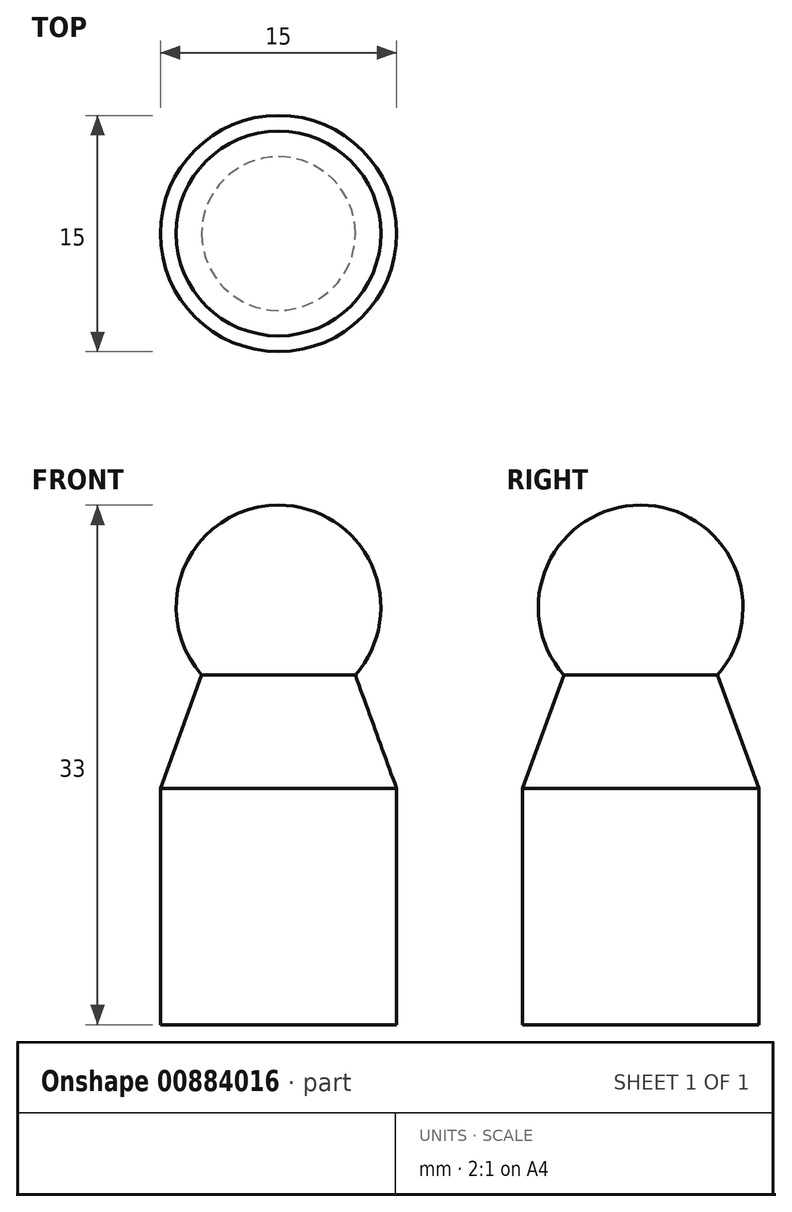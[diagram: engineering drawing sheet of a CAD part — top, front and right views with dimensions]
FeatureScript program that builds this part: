
annotation { "Feature Type Name" : "Feature", "Feature Type Description" : "" }
export const myFeature = defineFeature(function(context is Context, id is Id, definition is map)
    precondition{}
    {
        {
            var Q0;
            Q0=qCreatedBy(makeId("Top.planeOp"),FACE);
            var sketch = newSketch(context, id + "F0", { "sketchPlane" : qUnion([Q0])});
            skCircle(sketch, "E0", {"center": v(0, 0) * mm, "radius": 7.5 * mm});
            skSolve(sketch);
        }
        {
            var Q0;
            Q0=qSketchRegion(id+"F0",true);
            extrude(context, id + "F1", {"entities" : qUnion([Q0]), "depth" : 15 * mm, "offsetDistance" : 25 * mm});
        }
        {
            var Q0;
            Q0=makeQuery(id+"F1.opExtrude","CAP_FACE",FACE,{"disambiguationData":[OSD([sQuery(id+"F0.wireOp",EDGE,"E0")])],"isStart":false});
            var Q1;
            Q1=qSketchRegion(id+"F3",true);
            extrude(context, id + "F2", {"entities" : qUnion([Q0, Q1]), "operationType" : NewBodyOperationType.ADD, "depth" : 10 * mm, "offsetDistance" : 25 * mm, "hasDraft" : true, "draftAngle" : 20 * degree, "draftPullDirection" : true});
        }
        {
            var Q0;
            Q0=qCreatedBy(makeId("Front.planeOp"),FACE);
            var sketch = newSketch(context, id + "F3", { "sketchPlane" : qUnion([Q0])});
            skArc(sketch, "E1", {"start": v(0, 20) * mm, "mid": v(6.5, 26.5) * mm, "end": v(0, 33) * mm});
            skLineSegment(sketch, "E2.0", {"start": v(-7.5, 15) * mm, "end": v(7.5, 15) * mm, "construction": true});
            skLineSegment(sketch, "E3", {"start": v(0, 20) * mm, "end": v(0, 33) * mm});
            skSolve(sketch);
        }
        {
            var Q0;
            Q0=qSketchRegion(id+"F3",true);
            var Q1;
            Q1=sQuery(id+"F3.wireOp",EDGE,"E3");
            revolve(context, id + "F4", {"operationType" : NewBodyOperationType.ADD, "entities" : qUnion([Q0]), "axis" : qUnion([Q1]), "revolveType" : RevolveType.FULL});
        }
    });
